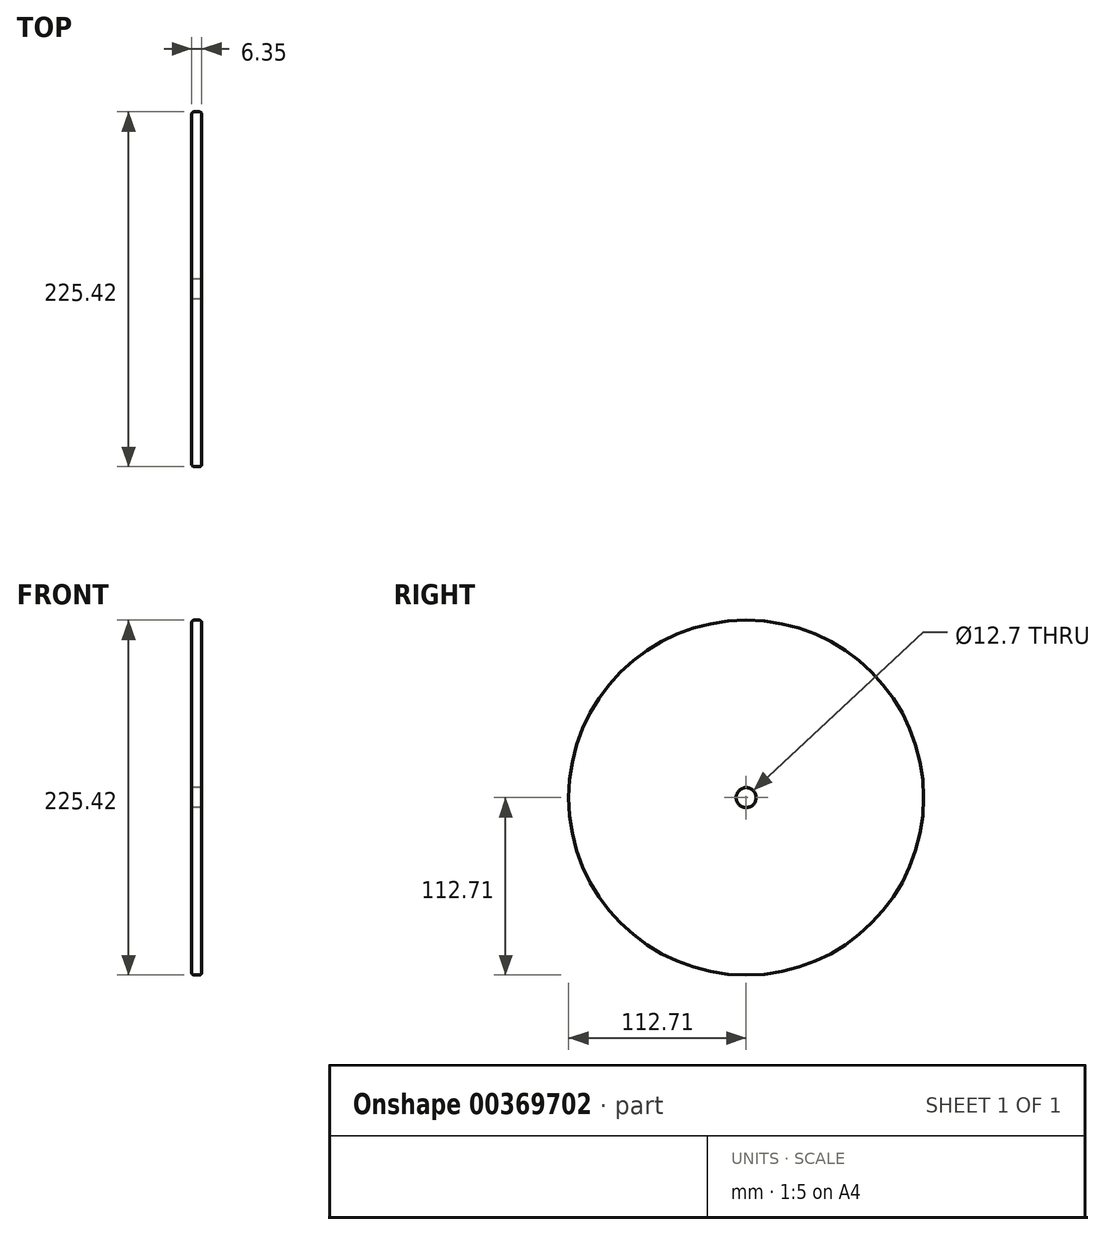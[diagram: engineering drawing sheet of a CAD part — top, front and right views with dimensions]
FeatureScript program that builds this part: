
annotation { "Feature Type Name" : "Feature", "Feature Type Description" : "" }
export const myFeature = defineFeature(function(context is Context, id is Id, definition is map)
    precondition{}
    {
        {
            var Q0;
            Q0=qCreatedBy(makeId("Right.planeOp"),FACE);
            var sketch = newSketch(context, id + "F0", { "sketchPlane" : qUnion([Q0])});
            skCircle(sketch, "E0", {"center": v(0, 0) * mm, "radius": 112.71 * mm});
            skCircle(sketch, "E1", {"center": v(0, 0) * mm, "radius": 6.35 * mm});
            skSolve(sketch);
        }
        {
            var Q0;
            Q0 = qSketchRegion(id + "F0", true);
            extrude(context, id + "F1", {"entities" : qUnion([Q0]), "depth" : 6.35 * mm, "offsetDistance" : 25.4 * mm});
        }
        {
            var Q0;
            Q0=makeQuery(id+"F1.opExtrude","CAP_EDGE",EDGE,{"disambiguationData":[OSD([sQuery(id+"F0.wireOp",EDGE,"E0")])],"isStart":true});
            var Q1;
            Q1=makeQuery(id+"F1.opExtrude","CAP_EDGE",EDGE,{"disambiguationData":[OSD([sQuery(id+"F0.wireOp",EDGE,"E0")])],"isStart":false});
            fillet(context, id + "F2", {"entities" : qUnion([Q0, Q1]), "radius" : 1.59 * mm, "tangentPropagation" : true, "allowEdgeOverflow" : false});
        }
    });
